# Revit family: Überspannungsableiter V20, 3-polig+NPE
name_source: partatom
category: Generic Models
revit_build: Autodesk Revit 2015 (Build: 20140606_1530(x64)
units: mm (PartAtom-declared; Revit-internal decimal feet)

## types (4) — shared parameters
Height = 79 mm
Length = 71 mm
Manufacturer = OBO Bettermann
Material = PA 66/6 FR HF RAL 9010
Material 2 = PA 66/6 FR HF RAL 2003
Material 3 = PA 66/6 FR HF RAL 5017
URL = http://www.obo-bettermann.com
Width = 90 mm  [stored 0.295276 ft]

## per-type parameters (varying)
| type | GTIN | Manufacturer Art.No. |
| V20-3+NPE-150 | 4012196163847 | 5095233 |
| V20-3+NPE-280 | 4012196161331 | 5095253 |
| V20-3+NPE-320 | 4012196161638 | 5095263 |
| V20-3+NPE-385 | 4012196161829 | 5095273 |

note: column(s) folded — value = type name in every type: Article Type

note: [stored X ft] marks values corroborated as IEEE doubles in the binary element streams (Revit-internal decimal feet)

## geometry (parser evidence)
native form markers: Sweep x1
no freeform markers — native parametric forms only
